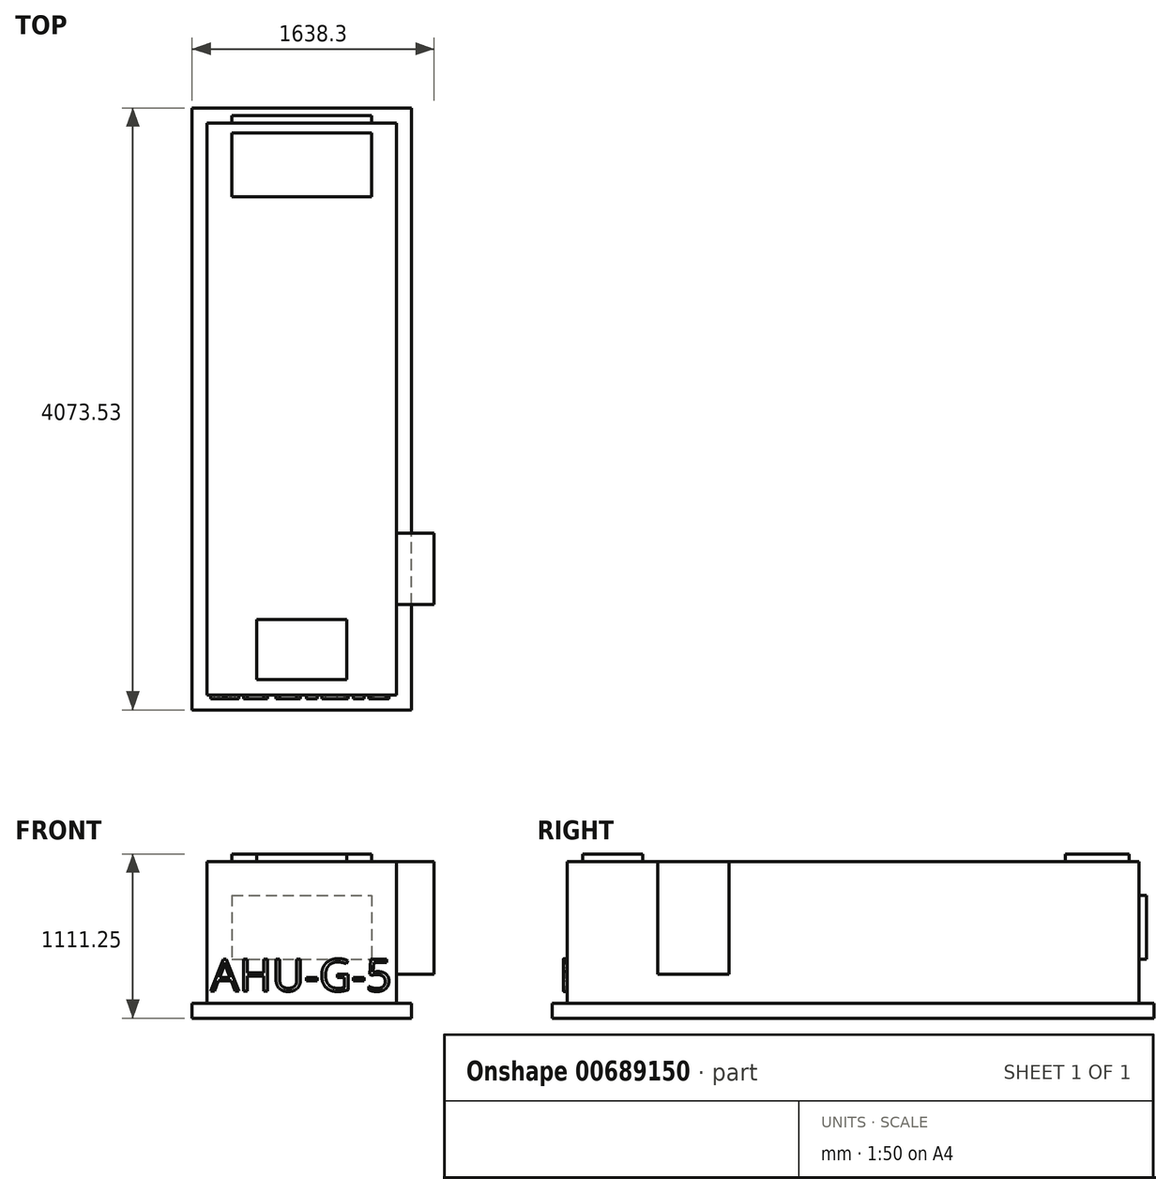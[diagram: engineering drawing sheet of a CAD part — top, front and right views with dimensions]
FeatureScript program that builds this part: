
annotation { "Feature Type Name" : "Feature", "Feature Type Description" : "" }
export const myFeature = defineFeature(function(context is Context, id is Id, definition is map)
    precondition{}
    {
        {
            var Q0;
            Q0=qCreatedBy(makeId("Front.planeOp"),FACE);
            var sketch = newSketch(context, id + "F0", { "sketchPlane" : qUnion([Q0])});
            skLineSegment(sketch, "E0.bottom", {"start": v(-639.94, 406.41) * mm, "end": v(642.76, 406.41) * mm});
            skLineSegment(sketch, "E0.top", {"start": v(-639.94, -552.44) * mm, "end": v(642.76, -552.44) * mm});
            skLineSegment(sketch, "E0.left", {"start": v(-639.94, 406.41) * mm, "end": v(-639.94, -552.44) * mm});
            skLineSegment(sketch, "E0.right", {"start": v(642.76, 406.41) * mm, "end": v(642.76, -552.44) * mm});
            skSolve(sketch);
        }
        {
            var Q0;
            Q0 = qSketchRegion(id + "F0", true);
            extrude(context, id + "F1", {"entities" : qUnion([Q0]), "depth" : 3870.32 * mm, "offsetDistance" : 25.4 * mm});
        }
        {
            var Q0;
            Q0=makeQuery(id+"F1.opExtrude","SWEPT_FACE",FACE,{"disambiguationData":[OSD([sQuery(id+"F0.wireOp",EDGE,"E0.bottom")])]});
            var sketch = newSketch(context, id + "F2", { "sketchPlane" : qUnion([Q0])});
            skLineSegment(sketch, "E1.bottom", {"start": v(-303.4, -3765.55) * mm, "end": v(306.2, -3765.55) * mm});
            skLineSegment(sketch, "E1.top", {"start": v(-303.4, -3359.15) * mm, "end": v(306.2, -3359.15) * mm});
            skLineSegment(sketch, "E1.left", {"start": v(-303.4, -3765.55) * mm, "end": v(-303.4, -3359.15) * mm});
            skLineSegment(sketch, "E1.right", {"start": v(306.2, -3765.55) * mm, "end": v(306.2, -3359.15) * mm});
            skSolve(sketch);
        }
        {
            var Q0;
            Q0 = qSketchRegion(id + "F2", true);
            extrude(context, id + "F3", {"entities" : qUnion([Q0]), "operationType" : NewBodyOperationType.ADD, "depth" : 50.8 * mm, "offsetDistance" : 25.4 * mm});
        }
        {
            var Q0;
            Q0=makeQuery(id+"F1.opExtrude","CAP_FACE",FACE,{"disambiguationData":[OSD([sQuery(id+"F0.wireOp",EDGE,"E0.bottom"),sQuery(id+"F0.wireOp",EDGE,"E0.top"),sQuery(id+"F0.wireOp",EDGE,"E0.left"),sQuery(id+"F0.wireOp",EDGE,"E0.right")])],"isStart":false});
            var sketch = newSketch(context, id + "F4", { "sketchPlane" : qUnion([Q0])});
            skLineSegment(sketch, "E2.bottom", {"start": v(-741.54, -552.44) * mm, "end": v(744.36, -552.44) * mm});
            skLineSegment(sketch, "E2.top", {"start": v(-741.54, -654.04) * mm, "end": v(744.36, -654.04) * mm});
            skLineSegment(sketch, "E2.left", {"start": v(-741.54, -552.44) * mm, "end": v(-741.54, -654.04) * mm});
            skLineSegment(sketch, "E2.right", {"start": v(744.36, -552.44) * mm, "end": v(744.36, -654.04) * mm});
            skSolve(sketch);
        }
        {
            var Q0;
            Q0 = qSketchRegion(id + "F4", true);
            extrude(context, id + "F5", {"entities" : qUnion([Q0]), "depth" : 101.6 * mm, "offsetDistance" : 25.4 * mm});
        }
        {
            var Q0;
            Q0=makeQuery(id+"F5.opExtrude","CAP_FACE",FACE,{"disambiguationData":[OSD([sQuery(id+"F4.wireOp",EDGE,"E2.bottom"),sQuery(id+"F4.wireOp",EDGE,"E2.top"),sQuery(id+"F4.wireOp",EDGE,"E2.left"),sQuery(id+"F4.wireOp",EDGE,"E2.right")])],"isStart":true});
            extrude(context, id + "F6", {"entities" : qUnion([Q0]), "operationType" : NewBodyOperationType.ADD, "depth" : 3971.92 * mm, "offsetDistance" : 25.4 * mm});
        }
        {
            var Q0;
            Q0=makeQuery(id+"F1.opExtrude","SWEPT_FACE",FACE,{"disambiguationData":[OSD([sQuery(id+"F0.wireOp",EDGE,"E0.right")])]});
            var sketch = newSketch(context, id + "F7", { "sketchPlane" : qUnion([Q0])});
            skLineSegment(sketch, "E3.bottom", {"start": v(-3257.55, 406.41) * mm, "end": v(-2774.95, 406.41) * mm});
            skLineSegment(sketch, "E3.top", {"start": v(-3257.55, -355.59) * mm, "end": v(-2774.95, -355.59) * mm});
            skLineSegment(sketch, "E3.left", {"start": v(-3257.55, 406.41) * mm, "end": v(-3257.55, -355.59) * mm});
            skLineSegment(sketch, "E3.right", {"start": v(-2774.95, 406.41) * mm, "end": v(-2774.95, -355.59) * mm});
            skSolve(sketch);
        }
        {
            var Q0;
            Q0 = qSketchRegion(id + "F7", true);
            extrude(context, id + "F8", {"entities" : qUnion([Q0]), "depth" : 254 * mm, "offsetDistance" : 25.4 * mm});
        }
        {
            var Q0;
            Q0=makeQuery(id+"F1.opExtrude","CAP_FACE",FACE,{"disambiguationData":[OSD([sQuery(id+"F0.wireOp",EDGE,"E0.bottom"),sQuery(id+"F0.wireOp",EDGE,"E0.top"),sQuery(id+"F0.wireOp",EDGE,"E0.left"),sQuery(id+"F0.wireOp",EDGE,"E0.right")])],"isStart":false});
            var sketch = newSketch(context, id + "F9", { "sketchPlane" : qUnion([Q0])});
            skText(sketch, "E4", { "text": "AHU-G-5", "fontName": "OpenSans-Regular.ttf"});
            const initialGuessF9  = {"E4": [-0.61556, -0.47083, 1, 0, 0.21805]};
            skSetInitialGuess(sketch, initialGuessF9);
            skSolve(sketch);
        }
        {
            var Q0;
            Q0 = qSketchRegion(id + "F9", true);
            extrude(context, id + "F10", {"entities" : qUnion([Q0]), "operationType" : NewBodyOperationType.ADD, "depth" : 25.4 * mm, "offsetDistance" : 25.4 * mm});
        }
        {
            var Q0;
            Q0=makeQuery(id+"F1.opExtrude","SWEPT_FACE",FACE,{"disambiguationData":[OSD([sQuery(id+"F0.wireOp",EDGE,"E0.bottom")])]});
            var sketch = newSketch(context, id + "F11", { "sketchPlane" : qUnion([Q0])});
            skLineSegment(sketch, "E5.bottom", {"start": v(-471.67, -498.47) * mm, "end": v(474.48, -498.47) * mm});
            skLineSegment(sketch, "E5.top", {"start": v(-471.67, -66.68) * mm, "end": v(474.48, -66.68) * mm});
            skLineSegment(sketch, "E5.left", {"start": v(-471.67, -498.48) * mm, "end": v(-471.67, -66.68) * mm});
            skLineSegment(sketch, "E5.right", {"start": v(474.48, -498.48) * mm, "end": v(474.48, -66.67) * mm});
            skSolve(sketch);
        }
        {
            var Q0;
            Q0 = qSketchRegion(id + "F11", true);
            extrude(context, id + "F12", {"entities" : qUnion([Q0]), "operationType" : NewBodyOperationType.ADD, "depth" : 50.8 * mm, "offsetDistance" : 25.4 * mm});
        }
        {
            var Q0;
            Q0=makeQuery(id+"F1.opExtrude","CAP_FACE",FACE,{"disambiguationData":[OSD([sQuery(id+"F0.wireOp",EDGE,"E0.bottom"),sQuery(id+"F0.wireOp",EDGE,"E0.top"),sQuery(id+"F0.wireOp",EDGE,"E0.left"),sQuery(id+"F0.wireOp",EDGE,"E0.right")])],"isStart":true});
            var sketch = newSketch(context, id + "F13", { "sketchPlane" : qUnion([Q0])});
            skLineSegment(sketch, "E6.bottom", {"start": v(471.67, 177.81) * mm, "end": v(-474.48, 177.81) * mm});
            skLineSegment(sketch, "E6.top", {"start": v(471.67, -253.99) * mm, "end": v(-474.48, -253.99) * mm});
            skLineSegment(sketch, "E6.left", {"start": v(471.67, 177.81) * mm, "end": v(471.67, -253.99) * mm});
            skLineSegment(sketch, "E6.right", {"start": v(-474.48, 177.81) * mm, "end": v(-474.48, -253.99) * mm});
            skSolve(sketch);
        }
        {
            var Q0;
            Q0 = qSketchRegion(id + "F13", true);
            extrude(context, id + "F14", {"entities" : qUnion([Q0]), "operationType" : NewBodyOperationType.ADD, "depth" : 50.8 * mm, "offsetDistance" : 25.4 * mm});
        }
    });
